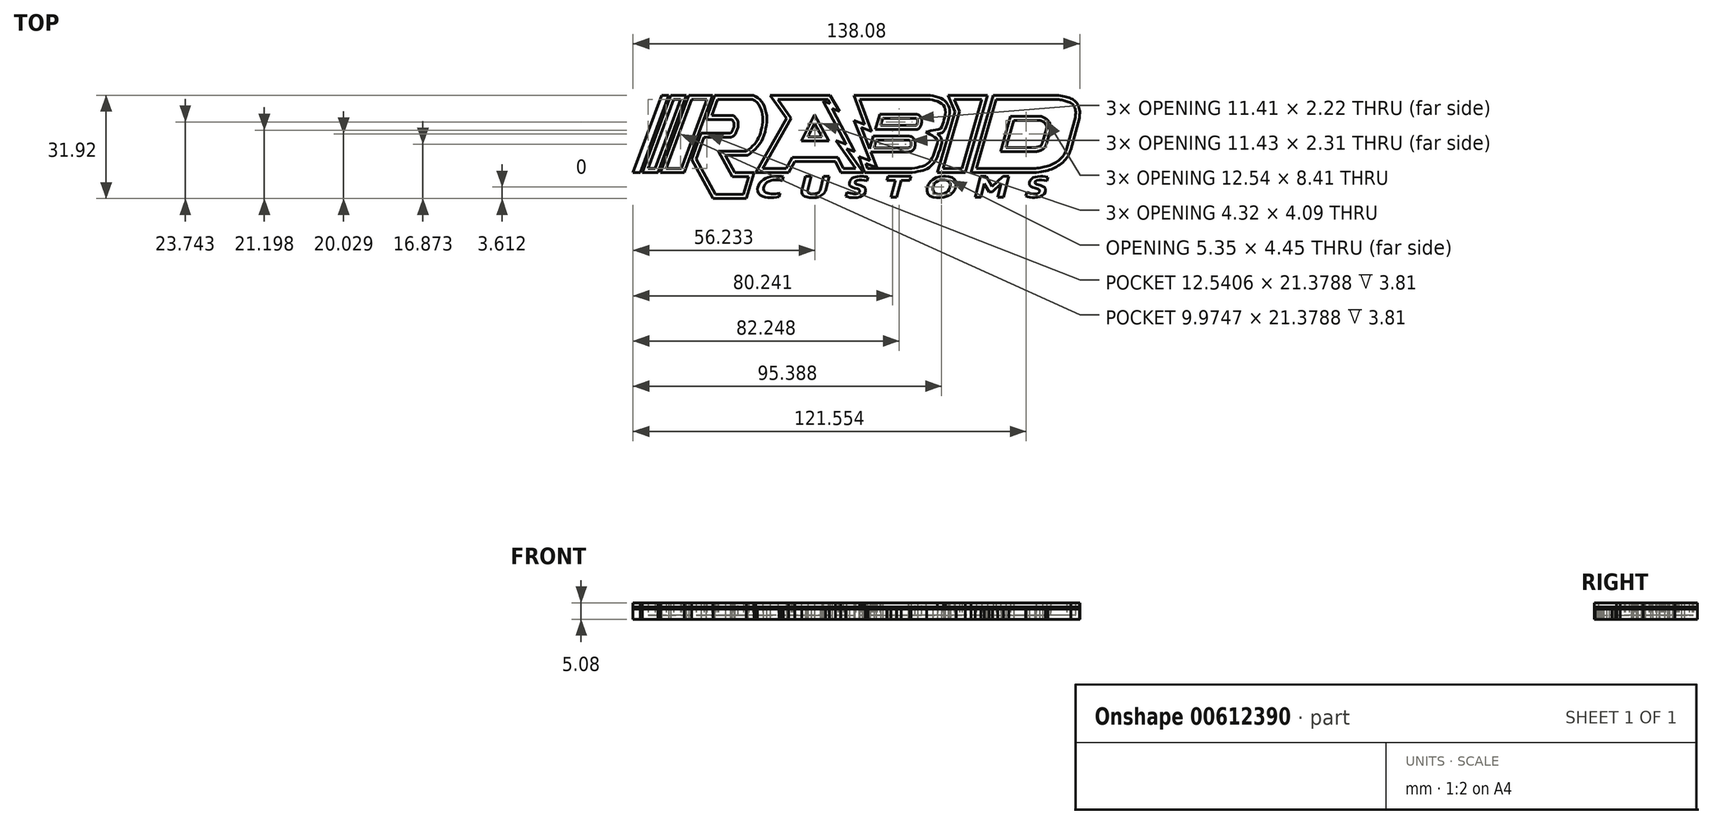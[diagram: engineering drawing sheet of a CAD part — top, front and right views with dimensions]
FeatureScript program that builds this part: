
annotation { "Feature Type Name" : "Feature", "Feature Type Description" : "" }
export const myFeature = defineFeature(function(context is Context, id is Id, definition is map)
    precondition{}
    {
        {
            var Q0;
            Q0=qCreatedBy(makeId("Top.planeOp"),FACE);
            var sketch = newSketch(context, id + "F0", { "sketchPlane" : qUnion([Q0])});
            skLineSegment(sketch, "E0", {"start": v(63.14, 15.4) * mm, "end": v(43.59, 15.4) * mm});
            skLineSegment(sketch, "E1", {"start": v(-67.72, -8.52) * mm, "end": v(-58.92, 15.4) * mm});
            skLineSegment(sketch, "E2", {"start": v(-51.92, -8.52) * mm, "end": v(-59.3, -8.52) * mm});
            skLineSegment(sketch, "E3", {"start": v(-56.72, 15.4) * mm, "end": v(-65.52, -8.52) * mm});
            skLineSegment(sketch, "E4", {"start": v(-64.84, -8.52) * mm, "end": v(-56.04, 15.4) * mm});
            skLineSegment(sketch, "E5", {"start": v(-51.23, 15.4) * mm, "end": v(-60.03, -8.52) * mm});
            skLineSegment(sketch, "E6", {"start": v(-59.3, -8.52) * mm, "end": v(-50.5, 15.4) * mm});
            skLineSegment(sketch, "E7", {"start": v(-43.12, 15.4) * mm, "end": v(-51.92, -8.52) * mm});
            skLineSegment(sketch, "E8", {"start": v(-45.2, 7.94) * mm, "end": v(-42.45, 15.4) * mm});
            skLineSegment(sketch, "E9", {"start": v(-45.2, 7.94) * mm, "end": v(-37.2, 7.94) * mm});
            skLineSegment(sketch, "E10", {"start": v(-37.63, 3.75) * mm, "end": v(-46.65, 3.75) * mm});
            skLineSegment(sketch, "E11", {"start": v(-46.65, 3.75) * mm, "end": v(-49.65, -4.39) * mm});
            skLineSegment(sketch, "E12", {"start": v(-49.65, -4.39) * mm, "end": v(-43.04, -16.52) * mm});
            skLineSegment(sketch, "E13", {"start": v(-43.04, -16.52) * mm, "end": v(-32.71, -16.52) * mm});
            skLineSegment(sketch, "E14", {"start": v(-32.71, -16.52) * mm, "end": v(-30.27, -8.46) * mm});
            skLineSegment(sketch, "E15", {"start": v(-30.27, -8.46) * mm, "end": v(-36.23, -8.46) * mm});
            skLineSegment(sketch, "E16", {"start": v(-36.23, -8.46) * mm, "end": v(-39.16, -3.08) * mm});
            skLineSegment(sketch, "E17", {"start": v(-39.16, -3.08) * mm, "end": v(-32.26, -3.08) * mm});
            skLineSegment(sketch, "E18", {"start": v(-29.78, -8.46) * mm, "end": v(-19.63, -8.46) * mm});
            skLineSegment(sketch, "E19", {"start": v(-25.33, 15.4) * mm, "end": v(-20.3, 8.28) * mm});
            skLineSegment(sketch, "E20", {"start": v(-20.3, 8.28) * mm, "end": v(-29.78, -8.46) * mm});
            skLineSegment(sketch, "E21", {"start": v(-19.63, -8.46) * mm, "end": v(-17.7, -5.04) * mm});
            skLineSegment(sketch, "E22", {"start": v(-17.7, -5.04) * mm, "end": v(-5.2, -5.04) * mm});
            skLineSegment(sketch, "E23", {"start": v(-5.2, -5.04) * mm, "end": v(-3.5, -8.46) * mm});
            skLineSegment(sketch, "E24", {"start": v(-6.75, 15.4) * mm, "end": v(-3.93, 10.47) * mm});
            skLineSegment(sketch, "E25", {"start": v(-3.93, 10.47) * mm, "end": v(-6.2, 11.32) * mm});
            skLineSegment(sketch, "E26", {"start": v(-6.2, 11.32) * mm, "end": v(0.84, -1.97) * mm});
            skLineSegment(sketch, "E27", {"start": v(0.84, -1.97) * mm, "end": v(-1.66, -1.06) * mm});
            skLineSegment(sketch, "E28", {"start": v(-1.66, -1.06) * mm, "end": v(3.5, -8.46) * mm});
            skLineSegment(sketch, "E29", {"start": v(-9.33, 2.63) * mm, "end": v(-13.65, 2.63) * mm});
            skLineSegment(sketch, "E30", {"start": v(-13.65, 2.63) * mm, "end": v(-11.6, 6.72) * mm});
            skLineSegment(sketch, "E31", {"start": v(-11.6, 6.72) * mm, "end": v(-9.33, 2.63) * mm});
            skLineSegment(sketch, "E32", {"start": v(0.59, 15.4) * mm, "end": v(3.85, 6.44) * mm});
            skLineSegment(sketch, "E33", {"start": v(3.85, 6.44) * mm, "end": v(0.55, 7.69) * mm});
            skLineSegment(sketch, "E34", {"start": v(0.55, 7.69) * mm, "end": v(5.5, -4.8) * mm});
            skLineSegment(sketch, "E35", {"start": v(5.5, -4.8) * mm, "end": v(2.03, -3.56) * mm});
            skLineSegment(sketch, "E36", {"start": v(2.03, -3.56) * mm, "end": v(3.9, -8.46) * mm});
            skLineSegment(sketch, "E37", {"start": v(9.47, 8.33) * mm, "end": v(8.82, 6.12) * mm});
            skLineSegment(sketch, "E38", {"start": v(6.8, -0.8) * mm, "end": v(17.35, -0.8) * mm});
            skLineSegment(sketch, "E39", {"start": v(7.48, 1.5) * mm, "end": v(17.6, 1.5) * mm});
            skLineSegment(sketch, "E40", {"start": v(9.47, 8.33) * mm, "end": v(19.75, 8.33) * mm});
            skLineSegment(sketch, "E41", {"start": v(8.82, 6.12) * mm, "end": v(19.5, 6.12) * mm});
            skLineSegment(sketch, "E42", {"start": v(29.63, 15.4) * mm, "end": v(31.86, 10.36) * mm});
            skLineSegment(sketch, "E43", {"start": v(31.86, 10.36) * mm, "end": v(26.4, -8.46) * mm});
            skLineSegment(sketch, "E44", {"start": v(41.79, 15.4) * mm, "end": v(34.96, -8.46) * mm});
            skLineSegment(sketch, "E45", {"start": v(43.59, 15.4) * mm, "end": v(36.77, -8.46) * mm});
            skLineSegment(sketch, "E46", {"start": v(57.72, 7.72) * mm, "end": v(49.97, 7.72) * mm});
            skLineSegment(sketch, "E47", {"start": v(49.97, 7.72) * mm, "end": v(47.56, -0.7) * mm});
            skLineSegment(sketch, "E48", {"start": v(47.56, -0.7) * mm, "end": v(56.76, -0.7) * mm});
            skLineSegment(sketch, "E49", {"start": v(60.1, 5.21) * mm, "end": v(58.87, 0.9) * mm});
            skFitSpline(sketch, "E50", {"points": [v(70.23, 8.37) * mm, v(70.23, 11.3) * mm, v(68.98, 13.62) * mm, v(67.2, 14.63) * mm, v(63.14, 15.4) * mm], "startDerivative": vector(1.44, 11.8) * mm, "endDerivative": vector(-15.36, 0) * mm});
            skLineSegment(sketch, "E51", {"start": v(70.23, 8.37) * mm, "end": v(67.61, -1.4) * mm});
            skFitSpline(sketch, "E52", {"points": [v(26.31, 3.48) * mm, v(27.66, 3.78) * mm, v(28.6, 4.72) * mm, v(30.1, 9.84) * mm, v(29.74, 12.25) * mm, v(28.71, 13.68) * mm, v(26.6, 14.85) * mm, v(23.32, 15.4) * mm], "startDerivative": vector(12.7, 2.15) * mm, "endDerivative": vector(-17.65, 0) * mm});
            skFitSpline(sketch, "E53", {"points": [v(26.31, 3.48) * mm, v(27.17, 2.79) * mm, v(27.7, 1.55) * mm, v(27.61, 0.35) * mm, v(25.8, -4.7) * mm, v(24.38, -6.43) * mm, v(22.74, -7.53) * mm, v(20.7, -8.07) * mm, v(17.69, -8.46) * mm], "startDerivative": vector(10.33, -6.33) * mm, "endDerivative": vector(-21.35, 0) * mm});
            skFitSpline(sketch, "E54", {"points": [v(19.75, 8.33) * mm, v(20.01, 8.2) * mm, v(20.22, 7.86) * mm, v(20.1, 6.56) * mm, v(19.95, 6.28) * mm, v(19.5, 6.12) * mm], "startDerivative": vector(1.94, 0) * mm, "endDerivative": vector(-2.82, 0) * mm});
            skFitSpline(sketch, "E55", {"points": [v(17.6, 1.5) * mm, v(17.93, 1.37) * mm, v(18.17, 0.96) * mm, v(18.18, -0.17) * mm, v(17.97, -0.55) * mm, v(17.35, -0.8) * mm], "startDerivative": vector(2.34, 0) * mm, "endDerivative": vector(-5.47, -0.56) * mm});
            skFitSpline(sketch, "E56", {"points": [v(-30.5, 15.4) * mm, v(-28.7, 14.3) * mm, v(-27.34, 12.4) * mm, v(-26.4, 9.2) * mm, v(-26.57, 5.78) * mm, v(-27.6, 2.09) * mm, v(-29.64, -0.93) * mm, v(-32.26, -3.08) * mm], "startDerivative": vector(16.3, -8.18) * mm, "endDerivative": vector(-18.4, -13.35) * mm});
            skFitSpline(sketch, "E57", {"points": [v(57.72, 7.72) * mm, v(58.57, 7.52) * mm, v(59.23, 7.13) * mm, v(59.76, 6.54) * mm, v(60.1, 5.21) * mm], "startDerivative": vector(3.5, 0) * mm, "endDerivative": vector(-0.84, -6.8) * mm});
            skFitSpline(sketch, "E58", {"points": [v(56.76, -0.7) * mm, v(57.5, -0.52) * mm, v(58.2, -0.25) * mm, v(58.63, 0.26) * mm, v(58.87, 0.9) * mm], "startDerivative": vector(2.87, 0.64) * mm, "endDerivative": vector(0.84, 2.68) * mm});
            skLineSegment(sketch, "E59.trimOffspring", {"start": v(-56.72, 15.4) * mm, "end": v(-58.92, 15.4) * mm});
            skLineSegment(sketch, "E60.trimOffspring", {"start": v(-51.23, 15.4) * mm, "end": v(-56.04, 15.4) * mm});
            skLineSegment(sketch, "E61.trimOffspring", {"start": v(-43.12, 15.4) * mm, "end": v(-50.5, 15.4) * mm});
            skLineSegment(sketch, "E62.trimOffspring", {"start": v(-30.5, 15.4) * mm, "end": v(-42.45, 15.4) * mm});
            skLineSegment(sketch, "E63.trimOffspring", {"start": v(-60.03, -8.52) * mm, "end": v(-64.84, -8.52) * mm});
            skLineSegment(sketch, "E64.trimOffspring", {"start": v(-65.52, -8.52) * mm, "end": v(-67.72, -8.52) * mm});
            skLineSegment(sketch, "E65.trimOffspring", {"start": v(-3.5, -8.46) * mm, "end": v(3.5, -8.46) * mm});
            skLineSegment(sketch, "E66.trimOffspring", {"start": v(3.9, -8.46) * mm, "end": v(17.69, -8.46) * mm});
            skLineSegment(sketch, "E67.trimOffspring", {"start": v(-6.75, 15.4) * mm, "end": v(-25.33, 15.4) * mm});
            skLineSegment(sketch, "E68.trimOffspring", {"start": v(7.48, 1.5) * mm, "end": v(6.8, -0.8) * mm});
            skLineSegment(sketch, "E69.trimOffspring", {"start": v(23.32, 15.4) * mm, "end": v(0.59, 15.4) * mm});
            skLineSegment(sketch, "E70.trimOffspring", {"start": v(26.4, -8.46) * mm, "end": v(34.96, -8.46) * mm});
            skLineSegment(sketch, "E71.trimOffspring", {"start": v(36.77, -8.46) * mm, "end": v(56.13, -8.46) * mm});
            skLineSegment(sketch, "E72.trimOffspring", {"start": v(41.79, 15.4) * mm, "end": v(29.63, 15.4) * mm});
            skFitSpline(sketch, "E73", {"points": [v(67.61, -1.4) * mm, v(66.86, -3.06) * mm, v(65.63, -4.79) * mm, v(63.85, -6.28) * mm, v(61.91, -7.32) * mm, v(59.62, -7.97) * mm, v(56.13, -8.46) * mm], "startDerivative": vector(-4.7, -11.34) * mm, "endDerivative": vector(-18.16, 0) * mm});
            skLineSegment(sketch, "E74", {"start": v(-21.23, -9.76) * mm, "end": v(-21.5, -10.99) * mm});
            skFitSpline(sketch, "E75", {"points": [v(-21.5, -10.99) * mm, v(-22.97, -10.72) * mm, v(-24.28, -10.74) * mm, v(-25.85, -11.2) * mm, v(-27, -12.23) * mm, v(-27.37, -13.14) * mm, v(-27.28, -13.97) * mm, v(-26.77, -14.6) * mm, v(-25.82, -14.94) * mm, v(-24.18, -15.08) * mm, v(-22.33, -14.83) * mm], "startDerivative": vector(-13.97, 2.96) * mm, "endDerivative": vector(15.34, 2.82) * mm});
            skFitSpline(sketch, "E76", {"points": [v(-21.23, -9.76) * mm, v(-22.2, -9.6) * mm, v(-23.42, -9.55) * mm, v(-24.64, -9.6) * mm, v(-26.04, -9.93) * mm, v(-26.99, -10.35) * mm, v(-27.96, -11) * mm, v(-28.75, -12) * mm, v(-29.08, -12.73) * mm, v(-29.23, -13.4) * mm, v(-29.15, -14.32) * mm, v(-28.73, -15.14) * mm, v(-27.9, -15.77) * mm, v(-26.68, -16.15) * mm, v(-25.33, -16.25) * mm, v(-23.8, -16.2) * mm, v(-22.58, -15.95) * mm], "startDerivative": vector(-16.16, 3.13) * mm, "endDerivative": vector(17.8, 4.48) * mm});
            skLineSegment(sketch, "E77.trimOffspring", {"start": v(-22.33, -14.83) * mm, "end": v(-22.58, -15.95) * mm});
            skLineSegment(sketch, "E78", {"start": v(-14.42, -9.63) * mm, "end": v(-12.66, -9.63) * mm});
            skLineSegment(sketch, "E79", {"start": v(12.2, -16.1) * mm, "end": v(13.8, -16.1) * mm});
            skLineSegment(sketch, "E80", {"start": v(-14.42, -9.63) * mm, "end": v(-15.45, -13.6) * mm});
            skLineSegment(sketch, "E81", {"start": v(-12.66, -9.63) * mm, "end": v(-13.72, -13.7) * mm});
            skLineSegment(sketch, "E82", {"start": v(-8.8, -9.63) * mm, "end": v(-9.9, -13.88) * mm});
            skLineSegment(sketch, "E83", {"start": v(-7.1, -9.63) * mm, "end": v(-8.22, -14.01) * mm});
            skFitSpline(sketch, "E84", {"points": [v(-15.45, -13.6) * mm, v(-15.56, -14.25) * mm, v(-15.45, -14.91) * mm, v(-15.19, -15.4) * mm, v(-14.47, -15.9) * mm, v(-13.08, -16.2) * mm, v(-11.72, -16.22) * mm, v(-10.7, -16.06) * mm, v(-9.8, -15.69) * mm, v(-8.93, -15.06) * mm, v(-8.47, -14.55) * mm, v(-8.22, -14.01) * mm], "startDerivative": vector(-1.99, -8.13) * mm, "endDerivative": vector(2.8, 7.52) * mm});
            skFitSpline(sketch, "E85", {"points": [v(-13.72, -13.7) * mm, v(-13.77, -13.94) * mm, v(-13.77, -14.2) * mm, v(-13.72, -14.43) * mm, v(-13.43, -14.76) * mm, v(-12.93, -14.99) * mm, v(-11.88, -15.05) * mm, v(-11.08, -14.96) * mm, v(-10.47, -14.73) * mm, v(-10.11, -14.34) * mm, v(-9.9, -13.88) * mm], "startDerivative": vector(-0.84, -3.35) * mm, "endDerivative": vector(1.84, 4.68) * mm});
            skLineSegment(sketch, "E86.trimOffspring", {"start": v(-8.8, -9.63) * mm, "end": v(-7.1, -9.63) * mm});
            skLineSegment(sketch, "E87", {"start": v(4.85, -9.89) * mm, "end": v(4.6, -11.04) * mm});
            skFitSpline(sketch, "E88", {"points": [v(4.6, -11.04) * mm, v(3.56, -10.81) * mm, v(2.6, -10.7) * mm, v(1.85, -10.74) * mm, v(1.26, -10.94) * mm, v(1, -11.17) * mm, v(0.94, -11.35) * mm, v(0.93, -11.6) * mm, v(1.06, -11.85) * mm, v(1.45, -12.06) * mm, v(2.83, -12.5) * mm, v(3.5, -12.8) * mm, v(3.91, -13.1) * mm, v(4.11, -13.37) * mm, v(4.17, -13.67) * mm, v(4.17, -14.01) * mm, v(4.02, -14.62) * mm, v(3.54, -15.3) * mm, v(2.88, -15.77) * mm, v(2.05, -16.06) * mm, v(0.97, -16.24) * mm, v(0.23, -16.27) * mm, v(-0.68, -16.14) * mm, v(-1.44, -15.96) * mm, v(-1.98, -15.77) * mm], "startDerivative": vector(-19.24, 4.6) * mm, "endDerivative": vector(-13.06, 4.98) * mm});
            skFitSpline(sketch, "E89", {"points": [v(4.85, -9.89) * mm, v(4.17, -9.74) * mm, v(3.28, -9.63) * mm, v(2.3, -9.63) * mm, v(1.36, -9.74) * mm, v(0.64, -9.93) * mm, v(0.14, -10.19) * mm, v(-0.27, -10.55) * mm, v(-0.68, -11.1) * mm, v(-0.87, -11.73) * mm, v(-0.72, -12.43) * mm, v(-0.15, -12.87) * mm, v(0.52, -13.13) * mm, v(1.58, -13.47) * mm, v(2.06, -13.67) * mm, v(2.33, -14) * mm, v(2.36, -14.28) * mm, v(2.25, -14.6) * mm, v(1.98, -14.81) * mm, v(1.59, -14.98) * mm, v(0.9, -15.06) * mm, v(0.29, -15.02) * mm, v(-0.54, -14.88) * mm, v(-1.25, -14.69) * mm, v(-1.63, -14.5) * mm], "startDerivative": vector(-14.34, 3.67) * mm, "endDerivative": vector(-10.03, 5.5) * mm});
            skLineSegment(sketch, "E90", {"start": v(-1.63, -14.5) * mm, "end": v(-1.98, -15.77) * mm});
            skLineSegment(sketch, "E91", {"start": v(60.47, -9.88) * mm, "end": v(60.23, -11.03) * mm});
            skFitSpline(sketch, "E92", {"points": [v(60.23, -11.03) * mm, v(59.18, -10.8) * mm, v(58.22, -10.69) * mm, v(57.47, -10.73) * mm, v(56.88, -10.93) * mm, v(56.62, -11.16) * mm, v(56.56, -11.34) * mm, v(56.55, -11.6) * mm, v(56.68, -11.84) * mm, v(57.07, -12.06) * mm, v(58.45, -12.5) * mm, v(59.12, -12.8) * mm, v(59.53, -13.08) * mm, v(59.73, -13.36) * mm, v(59.79, -13.67) * mm, v(59.79, -14) * mm, v(59.64, -14.61) * mm, v(59.16, -15.29) * mm, v(58.5, -15.76) * mm, v(57.67, -16.06) * mm, v(56.59, -16.24) * mm, v(55.85, -16.26) * mm, v(54.94, -16.13) * mm, v(54.19, -15.95) * mm, v(53.64, -15.76) * mm], "startDerivative": vector(-19.24, 4.6) * mm, "endDerivative": vector(-13.06, 4.98) * mm});
            skFitSpline(sketch, "E93", {"points": [v(60.47, -9.88) * mm, v(59.79, -9.73) * mm, v(58.9, -9.62) * mm, v(57.92, -9.62) * mm, v(56.98, -9.73) * mm, v(56.26, -9.92) * mm, v(55.76, -10.18) * mm, v(55.35, -10.54) * mm, v(54.94, -11.1) * mm, v(54.75, -11.73) * mm, v(54.9, -12.43) * mm, v(55.47, -12.86) * mm, v(56.14, -13.12) * mm, v(57.2, -13.46) * mm, v(57.68, -13.67) * mm, v(57.95, -14) * mm, v(57.99, -14.27) * mm, v(57.87, -14.6) * mm, v(57.6, -14.8) * mm, v(57.2, -14.97) * mm, v(56.52, -15.05) * mm, v(55.91, -15) * mm, v(55.08, -14.87) * mm, v(54.37, -14.68) * mm, v(54, -14.5) * mm], "startDerivative": vector(-14.34, 3.67) * mm, "endDerivative": vector(-10.03, 5.5) * mm});
            skLineSegment(sketch, "E94", {"start": v(54, -14.5) * mm, "end": v(53.64, -15.76) * mm});
            skLineSegment(sketch, "E95", {"start": v(11.08, -9.63) * mm, "end": v(10.77, -10.85) * mm});
            skLineSegment(sketch, "E96", {"start": v(10.77, -10.85) * mm, "end": v(13.42, -10.85) * mm});
            skLineSegment(sketch, "E97", {"start": v(13.42, -10.85) * mm, "end": v(12.02, -16.1) * mm});
            skLineSegment(sketch, "E98", {"start": v(12.02, -16.1) * mm, "end": v(12.2, -16.1) * mm});
            skLineSegment(sketch, "E99", {"start": v(13.8, -16.1) * mm, "end": v(15.2, -10.85) * mm});
            skLineSegment(sketch, "E100", {"start": v(15.2, -10.85) * mm, "end": v(17.86, -10.85) * mm});
            skLineSegment(sketch, "E101", {"start": v(17.86, -10.85) * mm, "end": v(18.16, -9.63) * mm});
            skFitSpline(sketch, "E102", {"points": [v(27.98, -10.68) * mm, v(27.19, -10.76) * mm, v(26.47, -11.02) * mm, v(25.85, -11.42) * mm, v(25.4, -11.93) * mm, v(25.08, -12.64) * mm, v(24.92, -13.24) * mm, v(24.96, -14) * mm, v(25.34, -14.58) * mm, v(25.9, -14.94) * mm, v(26.64, -15.1) * mm, v(27.47, -15.13) * mm, v(28.26, -14.98) * mm, v(29.06, -14.64) * mm, v(29.68, -14.13) * mm, v(30.1, -13.5) * mm, v(30.34, -12.7) * mm, v(30.37, -12.02) * mm, v(30.16, -11.45) * mm, v(29.8, -11.09) * mm, v(29.2, -10.83) * mm, v(28.61, -10.7) * mm, v(27.98, -10.68) * mm]});
            skFitSpline(sketch, "E103", {"points": [v(28.21, -9.63) * mm, v(27.44, -9.67) * mm, v(26.74, -9.79) * mm, v(25.84, -10.1) * mm, v(25.14, -10.46) * mm, v(24.5, -10.9) * mm, v(24.01, -11.4) * mm, v(23.65, -11.96) * mm, v(23.35, -12.55) * mm, v(23.16, -13.25) * mm, v(23.1, -13.88) * mm, v(23.2, -14.57) * mm, v(23.4, -15.05) * mm, v(23.77, -15.47) * mm, v(24.22, -15.73) * mm, v(24.84, -15.98) * mm, v(25.5, -16.1) * mm, v(26.21, -16.15) * mm, v(27.08, -16.16) * mm, v(27.82, -16.14) * mm, v(28.85, -15.98) * mm, v(29.51, -15.73) * mm, v(30.26, -15.31) * mm, v(30.74, -15) * mm, v(31.25, -14.48) * mm, v(31.62, -13.96) * mm, v(31.88, -13.45) * mm, v(32.09, -12.75) * mm, v(32.2, -11.83) * mm, v(32.03, -11.08) * mm, v(31.72, -10.64) * mm, v(31.26, -10.26) * mm, v(30.72, -9.98) * mm, v(30.04, -9.77) * mm, v(29.55, -9.68) * mm, v(28.95, -9.63) * mm, v(28.21, -9.63) * mm]});
            skLineSegment(sketch, "E104", {"start": v(39.69, -9.63) * mm, "end": v(38.06, -16.1) * mm});
            skLineSegment(sketch, "E105", {"start": v(40.82, -11.93) * mm, "end": v(39.76, -16.1) * mm});
            skLineSegment(sketch, "E106", {"start": v(41.43, -9.63) * mm, "end": v(43.29, -12.74) * mm});
            skLineSegment(sketch, "E107", {"start": v(43.29, -12.74) * mm, "end": v(46.71, -9.63) * mm});
            skLineSegment(sketch, "E108", {"start": v(48.4, -9.63) * mm, "end": v(46.78, -16.1) * mm});
            skLineSegment(sketch, "E109", {"start": v(40.82, -11.93) * mm, "end": v(42.29, -14.4) * mm});
            skLineSegment(sketch, "E110", {"start": v(42.29, -14.4) * mm, "end": v(43.35, -14.4) * mm});
            skLineSegment(sketch, "E111", {"start": v(43.35, -14.4) * mm, "end": v(46.08, -11.91) * mm});
            skLineSegment(sketch, "E112", {"start": v(46.08, -11.91) * mm, "end": v(45.03, -16.1) * mm});
            skLineSegment(sketch, "E113.trimOffspring", {"start": v(46.71, -9.63) * mm, "end": v(48.4, -9.63) * mm});
            skLineSegment(sketch, "E114.trimOffspring", {"start": v(45.03, -16.1) * mm, "end": v(46.78, -16.1) * mm});
            skLineSegment(sketch, "E115.trimOffspring", {"start": v(39.69, -9.63) * mm, "end": v(41.43, -9.63) * mm});
            skLineSegment(sketch, "E116.trimOffspring", {"start": v(38.06, -16.1) * mm, "end": v(39.76, -16.1) * mm});
            skLineSegment(sketch, "E117.trimOffspring", {"start": v(28.21, -9.63) * mm, "end": v(28.95, -9.63) * mm});
            skLineSegment(sketch, "E118.trimOffspring", {"start": v(11.08, -9.63) * mm, "end": v(18.16, -9.63) * mm});
            skLineSegment(sketch, "E119.trimOffspring", {"start": v(2.3, -9.63) * mm, "end": v(3.28, -9.63) * mm});
            skFitSpline(sketch, "E120", {"points": [v(-37.2, 7.94) * mm, v(-36.54, 6.97) * mm, v(-36.58, 5.6) * mm, v(-37.2, 4.16) * mm, v(-37.63, 3.75) * mm], "startDerivative": vector(3.16, -3.56) * mm, "endDerivative": vector(-2.38, -1.75) * mm});
            skSolve(sketch);
        }
        {
            var Q0;
            Q0=makeQuery(id+"F0.imprint","IMPRINT",FACE,{"disambiguationData":[TD([[makeQuery(id+"F0.imprint","IMPRINT",EDGE,{"derivedFrom":sQuery(id+"F0.wireOp",EDGE,"E1")}),-1.0]])]});
            var Q1;
            Q1=makeQuery(id+"F0.imprint","IMPRINT",FACE,{"disambiguationData":[TD([[makeQuery(id+"F0.imprint","IMPRINT",EDGE,{"derivedFrom":sQuery(id+"F0.wireOp",EDGE,"E2")}),-1.0]])]});
            var Q2;
            Q2=makeQuery(id+"F0.imprint","IMPRINT",FACE,{"disambiguationData":[TD([[makeQuery(id+"F0.imprint","IMPRINT",EDGE,{"derivedFrom":sQuery(id+"F0.wireOp",EDGE,"E4")}),-1.0]])]});
            var Q3;
            Q3=makeQuery(id+"F0.imprint","IMPRINT",FACE,{"disambiguationData":[TD([[makeQuery(id+"F0.imprint","IMPRINT",EDGE,{"derivedFrom":sQuery(id+"F0.wireOp",EDGE,"E8")}),-1.0]])]});
            var Q4;
            Q4=makeQuery(id+"F0.imprint","IMPRINT",FACE,{"disambiguationData":[TD([[makeQuery(id+"F0.imprint","IMPRINT",EDGE,{"derivedFrom":sQuery(id+"F0.wireOp",EDGE,"E42")}),1.0]])]});
            var Q5;
            Q5=makeQuery(id+"F0.imprint","IMPRINT",FACE,{"disambiguationData":[TD([[makeQuery(id+"F0.imprint","IMPRINT",EDGE,{"derivedFrom":sQuery(id+"F0.wireOp",EDGE,"E0")}),1.0]])]});
            var Q6;
            Q6=makeQuery(id+"F0.imprint","IMPRINT",FACE,{"disambiguationData":[TD([[makeQuery(id+"F0.imprint","IMPRINT",EDGE,{"derivedFrom":sQuery(id+"F0.wireOp",EDGE,"E18")}),1.0]])]});
            var Q7;
            {var subQ0=sQuery(id+"F0.wireOp",EDGE,"E119.trimOffspring");Q7=makeQuery(id+"F0.imprint","IMPRINT",FACE,{"disambiguationData":[TD([[makeQuery(id+"F0.imprint","IMPRINT",EDGE,{"derivedFrom":subQ0}),1.0]])]});}
            var Q8;
            {var subQ0=sQuery(id+"F0.wireOp",EDGE,"E117.trimOffspring");Q8=makeQuery(id+"F0.imprint","IMPRINT",FACE,{"disambiguationData":[TD([[makeQuery(id+"F0.imprint","IMPRINT",EDGE,{"derivedFrom":subQ0}),1.0]])]});}
            var Q9;
            Q9=makeQuery(id+"F0.imprint","IMPRINT",FACE,{"disambiguationData":[TD([[makeQuery(id+"F0.imprint","IMPRINT",EDGE,{"derivedFrom":sQuery(id+"F0.wireOp",EDGE,"E32")}),1.0]])]});
            extrude(context, id + "F1", {"entities" : qUnion([Q0, Q1, Q2, Q3, Q4, Q5, Q6, Q7, Q8, Q9]), "depth" : 5.08 * mm, "offsetDistance" : 25.4 * mm});
        }
        {
            var Q0;
            Q0=makeQuery(id+"F0.imprint","IMPRINT",FACE,{"disambiguationData":[TD([[makeQuery(id+"F0.imprint","IMPRINT",EDGE,{"derivedFrom":sQuery(id+"F0.wireOp",EDGE,"E1")}),-1.0]])]});
            var Q1;
            Q1=makeQuery(id+"F0.imprint","IMPRINT",FACE,{"disambiguationData":[TD([[makeQuery(id+"F0.imprint","IMPRINT",EDGE,{"derivedFrom":sQuery(id+"F0.wireOp",EDGE,"E2")}),-1.0]])]});
            var Q2;
            Q2=makeQuery(id+"F0.imprint","IMPRINT",FACE,{"disambiguationData":[TD([[makeQuery(id+"F0.imprint","IMPRINT",EDGE,{"derivedFrom":sQuery(id+"F0.wireOp",EDGE,"E4")}),-1.0]])]});
            var Q3;
            Q3=makeQuery(id+"F0.imprint","IMPRINT",FACE,{"disambiguationData":[TD([[makeQuery(id+"F0.imprint","IMPRINT",EDGE,{"derivedFrom":sQuery(id+"F0.wireOp",EDGE,"E8")}),-1.0]])]});
            var Q4;
            Q4=makeQuery(id+"F0.imprint","IMPRINT",FACE,{"disambiguationData":[TD([[makeQuery(id+"F0.imprint","IMPRINT",EDGE,{"derivedFrom":sQuery(id+"F0.wireOp",EDGE,"E42")}),1.0]])]});
            var Q5;
            Q5=makeQuery(id+"F0.imprint","IMPRINT",FACE,{"disambiguationData":[TD([[makeQuery(id+"F0.imprint","IMPRINT",EDGE,{"derivedFrom":sQuery(id+"F0.wireOp",EDGE,"E0")}),1.0]])]});
            var Q6;
            Q6=makeQuery(id+"F0.imprint","IMPRINT",FACE,{"disambiguationData":[TD([[makeQuery(id+"F0.imprint","IMPRINT",EDGE,{"derivedFrom":sQuery(id+"F0.wireOp",EDGE,"E18")}),1.0]])]});
            var Q7;
            {var subQ0=sQuery(id+"F0.wireOp",EDGE,"E119.trimOffspring");Q7=makeQuery(id+"F0.imprint","IMPRINT",FACE,{"disambiguationData":[TD([[makeQuery(id+"F0.imprint","IMPRINT",EDGE,{"derivedFrom":subQ0}),1.0]])]});}
            var Q8;
            {var subQ0=sQuery(id+"F0.wireOp",EDGE,"E117.trimOffspring");Q8=makeQuery(id+"F0.imprint","IMPRINT",FACE,{"disambiguationData":[TD([[makeQuery(id+"F0.imprint","IMPRINT",EDGE,{"derivedFrom":subQ0}),1.0]])]});}
            var Q9;
            Q9=makeQuery(id+"F0.imprint","IMPRINT",FACE,{"disambiguationData":[TD([[makeQuery(id+"F0.imprint","IMPRINT",EDGE,{"derivedFrom":sQuery(id+"F0.wireOp",EDGE,"E32")}),1.0]])]});
            extrude(context, id + "F2", {"entities" : qUnion([Q0, Q1, Q2, Q3, Q4, Q5, Q6, Q7, Q8, Q9]), "depth" : 3.8 * mm, "offsetDistance" : 25.4 * mm});
        }
        {
            var Q0;
            Q0=makeQuery(id+"F1.opExtrude","CAP_FACE",FACE,{"disambiguationData":[OSD([sQuery(id+"F0.wireOp",EDGE,"E8"),sQuery(id+"F0.wireOp",EDGE,"E9"),sQuery(id+"F0.wireOp",EDGE,"E10"),sQuery(id+"F0.wireOp",EDGE,"E11"),sQuery(id+"F0.wireOp",EDGE,"E12"),sQuery(id+"F0.wireOp",EDGE,"E13"),sQuery(id+"F0.wireOp",EDGE,"E14"),sQuery(id+"F0.wireOp",EDGE,"E15"),sQuery(id+"F0.wireOp",EDGE,"E16"),sQuery(id+"F0.wireOp",EDGE,"E17"),sQuery(id+"F0.wireOp",EDGE,"E56"),sQuery(id+"F0.wireOp",EDGE,"E62.trimOffspring"),sQuery(id+"F0.wireOp",EDGE,"E120")])],"isStart":false});
            var Q1;
            Q1=makeQuery(id+"F1.opExtrude","CAP_FACE",FACE,{"disambiguationData":[OSD([sQuery(id+"F0.wireOp",EDGE,"E18"),sQuery(id+"F0.wireOp",EDGE,"E19"),sQuery(id+"F0.wireOp",EDGE,"E20"),sQuery(id+"F0.wireOp",EDGE,"E21"),sQuery(id+"F0.wireOp",EDGE,"E22"),sQuery(id+"F0.wireOp",EDGE,"E23"),sQuery(id+"F0.wireOp",EDGE,"E24"),sQuery(id+"F0.wireOp",EDGE,"E25"),sQuery(id+"F0.wireOp",EDGE,"E26"),sQuery(id+"F0.wireOp",EDGE,"E27"),sQuery(id+"F0.wireOp",EDGE,"E28"),sQuery(id+"F0.wireOp",EDGE,"E29"),sQuery(id+"F0.wireOp",EDGE,"E30"),sQuery(id+"F0.wireOp",EDGE,"E31"),sQuery(id+"F0.wireOp",EDGE,"E65.trimOffspring"),sQuery(id+"F0.wireOp",EDGE,"E67.trimOffspring")])],"isStart":false});
            var Q2;
            Q2=makeQuery(id+"F1.opExtrude","CAP_FACE",FACE,{"disambiguationData":[OSD([sQuery(id+"F0.wireOp",EDGE,"E32"),sQuery(id+"F0.wireOp",EDGE,"E33"),sQuery(id+"F0.wireOp",EDGE,"E34"),sQuery(id+"F0.wireOp",EDGE,"E35"),sQuery(id+"F0.wireOp",EDGE,"E36"),sQuery(id+"F0.wireOp",EDGE,"E37"),sQuery(id+"F0.wireOp",EDGE,"E38"),sQuery(id+"F0.wireOp",EDGE,"E39"),sQuery(id+"F0.wireOp",EDGE,"E40"),sQuery(id+"F0.wireOp",EDGE,"E41"),sQuery(id+"F0.wireOp",EDGE,"E52"),sQuery(id+"F0.wireOp",EDGE,"E53"),sQuery(id+"F0.wireOp",EDGE,"E54"),sQuery(id+"F0.wireOp",EDGE,"E55"),sQuery(id+"F0.wireOp",EDGE,"E66.trimOffspring"),sQuery(id+"F0.wireOp",EDGE,"E68.trimOffspring"),sQuery(id+"F0.wireOp",EDGE,"E69.trimOffspring")])],"isStart":false});
            var Q3;
            Q3=makeQuery(id+"F1.opExtrude","CAP_FACE",FACE,{"disambiguationData":[OSD([sQuery(id+"F0.wireOp",EDGE,"E42"),sQuery(id+"F0.wireOp",EDGE,"E43"),sQuery(id+"F0.wireOp",EDGE,"E44"),sQuery(id+"F0.wireOp",EDGE,"E70.trimOffspring"),sQuery(id+"F0.wireOp",EDGE,"E72.trimOffspring")])],"isStart":false});
            var Q4;
            Q4=makeQuery(id+"F1.opExtrude","CAP_FACE",FACE,{"disambiguationData":[OSD([sQuery(id+"F0.wireOp",EDGE,"E0"),sQuery(id+"F0.wireOp",EDGE,"E45"),sQuery(id+"F0.wireOp",EDGE,"E46"),sQuery(id+"F0.wireOp",EDGE,"E47"),sQuery(id+"F0.wireOp",EDGE,"E48"),sQuery(id+"F0.wireOp",EDGE,"E49"),sQuery(id+"F0.wireOp",EDGE,"E50"),sQuery(id+"F0.wireOp",EDGE,"E51"),sQuery(id+"F0.wireOp",EDGE,"E57"),sQuery(id+"F0.wireOp",EDGE,"E58"),sQuery(id+"F0.wireOp",EDGE,"E71.trimOffspring"),sQuery(id+"F0.wireOp",EDGE,"E73")])],"isStart":false});
            var Q5;
            Q5=makeQuery(id+"F1.opExtrude","CAP_FACE",FACE,{"disambiguationData":[OSD([sQuery(id+"F0.wireOp",EDGE,"E2"),sQuery(id+"F0.wireOp",EDGE,"E6"),sQuery(id+"F0.wireOp",EDGE,"E7"),sQuery(id+"F0.wireOp",EDGE,"E61.trimOffspring")])],"isStart":false});
            var Q6;
            Q6=makeQuery(id+"F1.opExtrude","CAP_FACE",FACE,{"disambiguationData":[OSD([sQuery(id+"F0.wireOp",EDGE,"E4"),sQuery(id+"F0.wireOp",EDGE,"E5"),sQuery(id+"F0.wireOp",EDGE,"E60.trimOffspring"),sQuery(id+"F0.wireOp",EDGE,"E63.trimOffspring")])],"isStart":false});
            shell(context, id + "F3", {"entities" : qUnion([Q0, Q1, Q2, Q3, Q4, Q5, Q6]), "thickness" : 1.27 * mm});
        }
        {
            var Q0;
            Q0 = qSketchRegion(id + "F0", true);
            extrude(context, id + "F4", {"entities" : qUnion([Q0]), "depth" : 3.17 * mm, "offsetDistance" : 25.4 * mm});
        }
    });
